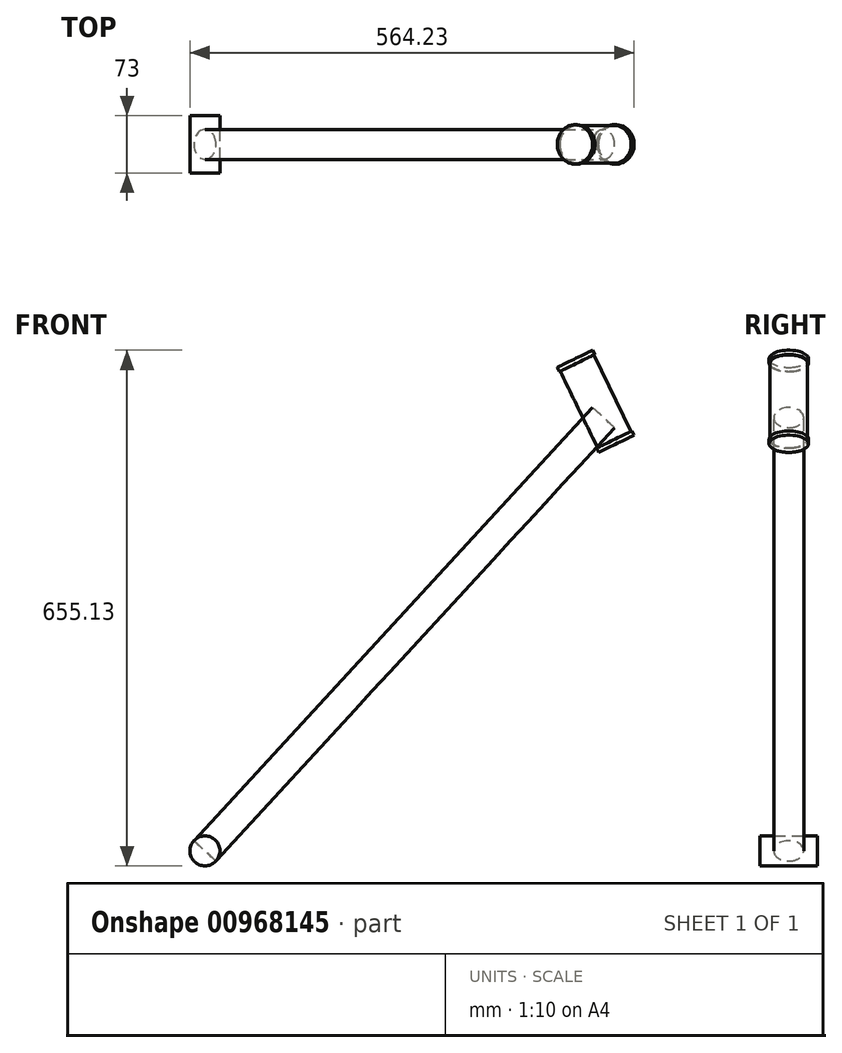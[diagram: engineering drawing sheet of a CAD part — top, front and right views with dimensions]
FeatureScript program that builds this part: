
annotation { "Feature Type Name" : "Feature", "Feature Type Description" : "" }
export const myFeature = defineFeature(function(context is Context, id is Id, definition is map)
    precondition{}
    {
        {
            var Q0;
            Q0=qCreatedBy(makeId("Front.planeOp"),FACE);
            var sketch = newSketch(context, id + "F0", { "sketchPlane" : qUnion([Q0])});
            skCircle(sketch, "E0", {"center": v(0, 0) * mm, "radius": 357 * mm});
            skLineSegment(sketch, "E1", {"start": v(420, 0) * mm, "end": v(420, -50) * mm});
            skLineSegment(sketch, "E2", {"start": v(420, -50) * mm, "end": v(290.45, 401.8) * mm});
            skLineSegment(sketch, "E3", {"start": v(420, -50) * mm, "end": v(420, 575) * mm});
            skLineSegment(sketch, "E4", {"start": v(420, 575) * mm, "end": v(890, 575) * mm});
            skLineSegment(sketch, "E5", {"start": v(890, 575) * mm, "end": v(942.6, 467.14) * mm});
            skLineSegment(sketch, "E6", {"start": v(942.6, 467.14) * mm, "end": v(1171.43, -2.03) * mm});
            skCircle(sketch, "E7", {"center": v(1171.43, -2.03) * mm, "radius": 357 * mm});
            skLineSegment(sketch, "E8", {"start": v(942.6, 467.14) * mm, "end": v(926.38, 500.4) * mm});
            skLineSegment(sketch, "E9", {"start": v(420, -50) * mm, "end": v(926.38, 500.4) * mm});
            skLineSegment(sketch, "E10", {"start": v(890, 575) * mm, "end": v(902.27, 549.83) * mm});
            skLineSegment(sketch, "E11", {"start": v(290.45, 401.8) * mm, "end": v(312.5, 324.9) * mm});
            skLineSegment(sketch, "E12", {"start": v(420, -50) * mm, "end": v(0, 0) * mm});
            skLineSegment(sketch, "E13", {"start": v(0, 0) * mm, "end": v(312.5, 324.9) * mm});
            skLineSegment(sketch, "E14", {"start": v(312.5, 324.9) * mm, "end": v(902.27, 549.83) * mm});
            skLineSegment(sketch, "E15", {"start": v(942.6, 467.14) * mm, "end": v(960.14, 431.2) * mm});
            skLineSegment(sketch, "E16", {"start": v(960.14, 431.2) * mm, "end": v(888.24, 396.12) * mm});
            skSolve(sketch);
        }
        {
            var Q0;
            Q0=sQuery(id+"F0.wireOp",VERTEX,"E1.end");
            var Q1;
            Q1=sQuery(id+"F0.wireOp",EDGE,"E9");
            cPlane(context, id + "F1", {"entities" : qUnion([Q0, Q1]), "cplaneType" : CPlaneType.LINE_POINT, "offset" : 25 * mm, "width" : 150 * mm, "height" : 150 * mm});
        }
        {
            var Q0;
            Q0=qCreatedBy(id+"F1.planeOp",FACE);
            var sketch = newSketch(context, id + "F2", { "sketchPlane" : qUnion([Q0])});
            skCircle(sketch, "E17", {"center": v(342.97, 0) * mm, "radius": 19.05 * mm});
            skSolve(sketch);
        }
        {
            var Q0;
            Q0=sQuery(id+"F0.wireOp",EDGE,"E5");
            var Q1;
            Q1=sQuery(id+"F0.wireOp",VERTEX,"E4.end");
            cPlane(context, id + "F3", {"entities" : qUnion([Q0, Q1]), "cplaneType" : CPlaneType.LINE_POINT, "offset" : 25 * mm, "width" : 150 * mm, "height" : 150 * mm});
        }
        {
            var Q0;
            Q0=qCreatedBy(id+"F3.planeOp",FACE);
            var sketch = newSketch(context, id + "F4", { "sketchPlane" : qUnion([Q0])});
            skCircle(sketch, "E18", {"center": v(1052.14, 0) * mm, "radius": 23.8 * mm});
            skCircle(sketch, "E19", {"center": v(1052.14, 0) * mm, "radius": 25 * mm});
            skSolve(sketch);
        }
        {
            var Q0;
            {var subQ0=sQuery(id+"F0.wireOp",EDGE,"E12");var subQ1=sQuery(id+"F0.wireOp",EDGE,"E0");var subQ2=makeQuery(id+"F0.imprint","INTERSECT",VERTEX,{"derivedFrom":[subQ1,subQ0]});Q0=makeQuery(id+"F0.imprint","IMPRINT",FACE,{"disambiguationData":[TD([[makeQuery(id+"F0.imprint","IMPRINT",EDGE,{"disambiguationData":[TD([[subQ2,1.0]])],"derivedFrom":subQ1}),1.0]])]});}
            var sketch = newSketch(context, id + "F5", { "sketchPlane" : qUnion([Q0])});
            skCircle(sketch, "E20", {"center": v(420.02, -50.06) * mm, "radius": 19.05 * mm});
            skSolve(sketch);
        }
        {
            var Q0;
            Q0=makeQuery(id+"F5.imprint","IMPRINT",FACE,{"disambiguationData":[TD([[makeQuery(id+"F5.imprint","IMPRINT",EDGE,{"derivedFrom":sQuery(id+"F5.wireOp",EDGE,"E20")}),1.0]])]});
            extrude(context, id + "F6", {"entities" : qUnion([Q0]), "endBound" : BoundingType.SYMMETRIC, "depth" : 73 * mm, "offsetDistance" : 25 * mm});
        }
        {
            var Q0;
            Q0=makeQuery(id+"F4.imprint","IMPRINT",FACE,{"disambiguationData":[TD([[makeQuery(id+"F4.imprint","IMPRINT",EDGE,{"derivedFrom":sQuery(id+"F4.wireOp",EDGE,"E18")}),-1.0]])]});
            extrude(context, id + "F7", {"entities" : qUnion([Q0]), "depth" : 120 * mm, "offsetDistance" : 25 * mm});
        }
        {
            var Q0;
            Q0=makeQuery(id+"F4.imprint","IMPRINT",FACE,{"disambiguationData":[TD([[makeQuery(id+"F4.imprint","IMPRINT",EDGE,{"derivedFrom":sQuery(id+"F4.wireOp",EDGE,"E18")}),1.0]])]});
            var Q1;
            Q1=makeQuery(id+"F4.imprint","IMPRINT",FACE,{"disambiguationData":[TD([[makeQuery(id+"F4.imprint","IMPRINT",EDGE,{"derivedFrom":sQuery(id+"F4.wireOp",EDGE,"E18")}),-1.0]])]});
            extrude(context, id + "F8", {"entities" : qUnion([Q0, Q1]), "operationType" : NewBodyOperationType.REMOVE, "depth" : 114 * mm, "offsetDistance" : 25 * mm});
        }
        {
            var Q0;
            Q0=makeQuery(id+"F4.imprint","IMPRINT",FACE,{"disambiguationData":[TD([[makeQuery(id+"F4.imprint","IMPRINT",EDGE,{"derivedFrom":sQuery(id+"F4.wireOp",EDGE,"E18")}),1.0]])]});
            extrude(context, id + "F9", {"entities" : qUnion([Q0]), "operationType" : NewBodyOperationType.ADD, "depth" : 120 * mm, "offsetDistance" : 25 * mm});
        }
        {
            var Q0;
            Q0=makeQuery(id+"F4.imprint","IMPRINT",FACE,{"disambiguationData":[TD([[makeQuery(id+"F4.imprint","IMPRINT",EDGE,{"derivedFrom":sQuery(id+"F4.wireOp",EDGE,"E18")}),-1.0]])]});
            extrude(context, id + "F10", {"entities" : qUnion([Q0]), "operationType" : NewBodyOperationType.ADD, "depth" : 6 * mm, "offsetDistance" : 25 * mm});
        }
        {
            var Q0;
            Q0 = qSketchRegion(id + "F2", true);
            var Q1;
            Q1=sQuery(id+"F0.wireOp",EDGE,"E9");
            sweep(context, id + "F11", {"profiles" : qUnion([Q0]), "path" : qUnion([Q1])});
        }
    });
